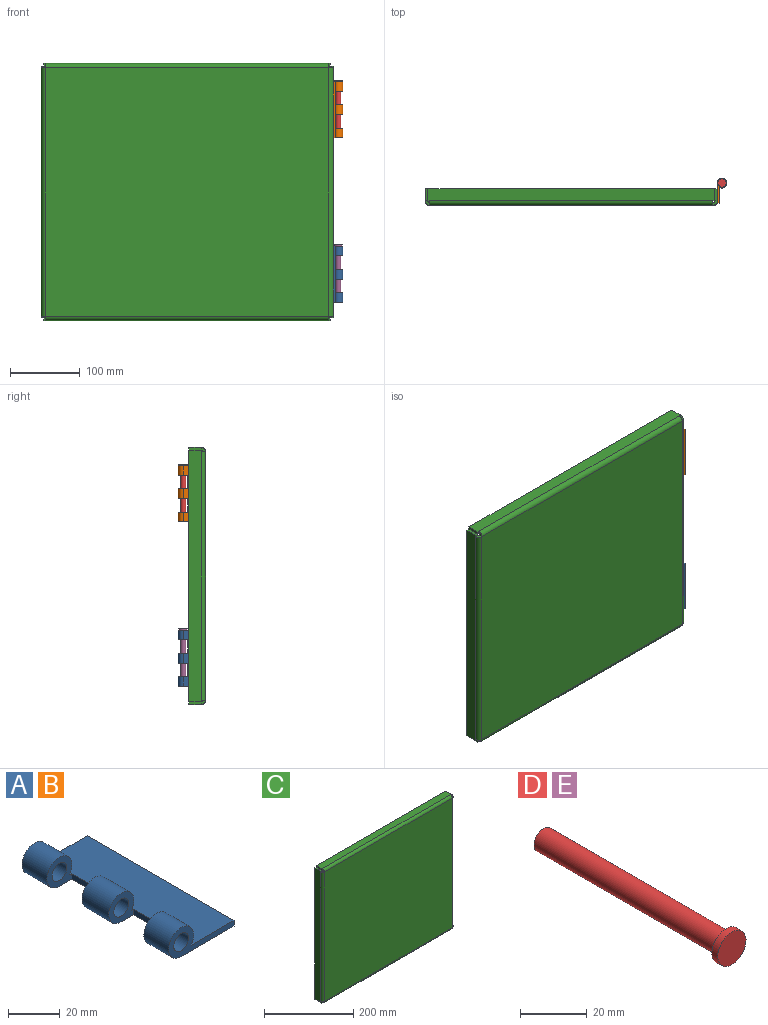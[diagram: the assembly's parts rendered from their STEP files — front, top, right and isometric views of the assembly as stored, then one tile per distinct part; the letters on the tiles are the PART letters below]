
ASSEMBLY  parts=5 mates=4
PART A: 17 faces, bbox 35.7x80x13.7 mm
  f0: plane 80x28.83mm, normal (0,0,-1), area 2044.6mm2, adj f2,f3,f5,f6,f8,f9,f10,f11
  f1: plane 80x23.43mm, normal (0,0,1), area 1819.5mm2, adj f2,f3,f5,f6,f8,f9,f10,f11
  f2: cylinder r=6.83mm len=14.6mm, axis (0,-1,0), area 535.2mm2, adj f0,f1,f12,f15
  f3: cylinder r=6.83mm len=13.65mm, axis (0,-1,0), area 494.8mm2, adj f0,f1,f9,f11
  f4: cylinder r=4.05mm len=13.5mm, axis (0,-1,0), area 343.5mm2, adj f9,f11
  f5: plane 80x2.65mm, normal (1,0,0), area 212mm2, adj f0,f1,f8,f9
  f6: cylinder r=6.83mm len=13.65mm, axis (0,-1,0), area 498.5mm2, adj f0,f1,f8,f14
  f7: cylinder r=4.05mm len=13.6mm, axis (0,-1,0), area 346.1mm2, adj f8,f14
  f8: plane 35.65x13.65mm, normal (0,1,0), area 161.2mm2, adj f0,f1,f5,f6,f7
  f9: plane 35.65x13.65mm, normal (0,-1,0), area 161.2mm2, adj f0,f1,f3,f4,f5
  f10: plane 19.15x2.65mm, normal (-1,0,0), area 50.7mm2, adj f0,f1,f11,f12
  f11: plane 13.65x13.65mm, normal (0,1,0), area 102.9mm2, adj f0,f1,f3,f4,f10
  f12: plane 13.65x13.65mm, normal (0,-1,0), area 102.9mm2, adj f0,f1,f2,f10,f16
  f13: plane 19.15x2.65mm, normal (-1,0,0), area 50.7mm2, adj f0,f1,f14,f15
  f14: plane 13.65x13.65mm, normal (0,-1,0), area 102.9mm2, adj f0,f1,f6,f7,f13
  f15: plane 13.65x13.65mm, normal (0,1,0), area 102.9mm2, adj f0,f1,f2,f13,f16
  f16: cylinder r=4.05mm len=14.6mm, axis (0,-1,0), area 371.5mm2, adj f12,f15
PART B: same geometry as A
PART C: 46 faces, bbox 418x24x368 mm
  f0: plane 4x2.28mm, normal (0,-1,0), area 9.1mm2, adj f4,f5,f6,f42
  f1: plane 4x2.28mm, normal (0,-1,0), area 9.1mm2, adj f2,f5,f6,f43
  f2: plane 17.7x4mm, normal (-1,0,0), area 70.8mm2, adj f1,f3,f5,f6
  f3: plane 409.96x4mm, normal (0,1,0), area 1639.8mm2, adj f2,f4,f5,f6
  f4: plane 17.7x4mm, normal (1,0,0), area 70.8mm2, adj f0,f3,f5,f6
  f5: plane 409.96x17.7mm, normal (0,0,-1), area 7256.3mm2, adj f0,f1,f2,f3,f4,f44
  f6: plane 409.96x17.7mm, normal (0,0,1), area 7256.3mm2, adj f0,f1,f2,f3,f4,f45
  f7: plane 405.4x355.4mm, normal (0,-1,0), area 144079.2mm2, adj f18,f29,f40,f44
  f8: plane 405.4x355.4mm, normal (0,1,0), area 144079.2mm2, adj f19,f30,f41,f45
  f9: plane 4x2.28mm, normal (0,-1,0), area 9.1mm2, adj f13,f14,f15,f17
  f10: plane 4x2.28mm, normal (0,-1,0), area 9.1mm2, adj f11,f14,f15,f16
  f11: plane 17.7x4mm, normal (1,0,0), area 70.8mm2, adj f10,f12,f14,f15
  f12: plane 409.96x4mm, normal (0,1,0), area 1639.8mm2, adj f11,f13,f14,f15
  f13: plane 17.7x4mm, normal (-1,0,0), area 70.8mm2, adj f9,f12,f14,f15
  f14: plane 409.96x17.7mm, normal (0,0,1), area 7256.3mm2, adj f9,f10,f11,f12,f13,f18
  f15: plane 409.96x17.7mm, normal (0,0,-1), area 7256.3mm2, adj f9,f10,f11,f12,f13,f19
  f16: plane 6.3x6.3mm, normal (1,0,0), area 27mm2, adj f10,f18,f19,f38
  f17: plane 6.3x6.3mm, normal (-1,0,0), area 27mm2, adj f9,f18,f19,f27
  f18: cylinder r=6.3mm len=405.4mm, axis (1,0,0), area 4011.8mm2, adj f7,f14,f16,f17
  f19: cylinder r=2.3mm len=405.4mm, axis (1,0,0), area 1464.6mm2, adj f8,f15,f16,f17
  f20: plane 4x2.28mm, normal (0,-1,0), area 9.1mm2, adj f24,f25,f26,f28
  f21: plane 4x2.28mm, normal (0,-1,0), area 9.1mm2, adj f22,f25,f26,f27
  f22: plane 17.7x4mm, normal (0,0,1), area 70.8mm2, adj f21,f23,f25,f26
  f23: plane 359.96x4mm, normal (0,1,0), area 1439.8mm2, adj f22,f24,f25,f26
  f24: plane 17.7x4mm, normal (0,0,-1), area 70.8mm2, adj f20,f23,f25,f26
  f25: plane 359.96x17.7mm, normal (-1,0,0), area 6371.3mm2, adj f20,f21,f22,f23,f24,f29
  f26: plane 359.96x17.7mm, normal (1,0,0), area 6371.3mm2, adj f20,f21,f22,f23,f24,f30
  f27: plane 6.3x6.3mm, normal (0,0,1), area 27mm2, adj f17,f21,f29,f30
  f28: plane 6.3x6.3mm, normal (0,0,-1), area 27mm2, adj f20,f29,f30,f43
  f29: cylinder r=6.3mm len=355.4mm, axis (0,0,1), area 3517mm2, adj f7,f25,f27,f28
  f30: cylinder r=2.3mm len=355.4mm, axis (0,0,1), area 1284mm2, adj f8,f26,f27,f28
  f31: plane 4x2.28mm, normal (0,-1,0), area 9.1mm2, adj f35,f36,f37,f38
  f32: plane 4x2.28mm, normal (0,-1,0), area 9.1mm2, adj f33,f36,f37,f39
  f33: plane 17.7x4mm, normal (0,0,-1), area 70.8mm2, adj f32,f34,f36,f37
  f34: plane 359.96x4mm, normal (0,1,0), area 1439.8mm2, adj f33,f35,f36,f37
  f35: plane 17.7x4mm, normal (0,0,1), area 70.8mm2, adj f31,f34,f36,f37
  f36: plane 359.96x17.7mm, normal (1,0,0), area 6371.3mm2, adj f31,f32,f33,f34,f35,f40
  f37: plane 359.96x17.7mm, normal (-1,0,0), area 6371.3mm2, adj f31,f32,f33,f34,f35,f41
  f38: plane 6.3x6.3mm, normal (0,0,1), area 27mm2, adj f16,f31,f40,f41
  f39: plane 6.3x6.3mm, normal (0,0,-1), area 27mm2, adj f32,f40,f41,f42
  f40: cylinder r=6.3mm len=355.4mm, axis (0,0,1), area 3517mm2, adj f7,f36,f38,f39
  f41: cylinder r=2.3mm len=355.4mm, axis (0,0,1), area 1284mm2, adj f8,f37,f38,f39
  f42: plane 6.3x6.3mm, normal (1,0,0), area 27mm2, adj f0,f39,f44,f45
  f43: plane 6.3x6.3mm, normal (-1,0,0), area 27mm2, adj f1,f28,f44,f45
  f44: cylinder r=6.3mm len=405.4mm, axis (1,0,0), area 4011.8mm2, adj f5,f7,f42,f43
  f45: cylinder r=2.3mm len=405.4mm, axis (1,0,0), area 1464.6mm2, adj f6,f8,f42,f43
PART D: 5 faces, bbox 12x80x12 mm
  f0: cylinder r=4mm len=77.5mm, axis (0,1,0), area 1947.8mm2, adj f1,f4
  f1: plane 8x8mm, normal (0,1,0), area 50.3mm2, adj f0
  f2: cylinder r=6mm len=12mm, axis (0,1,0), area 94.2mm2, adj f3,f4
  f3: plane 12x12mm, normal (0,-1,0), area 113.1mm2, adj f2
  f4: plane 12x12mm, normal (0,1,0), area 62.8mm2, adj f0,f2
PART E: same geometry as D
PLACE A rot(axis=(-0.58,0.58,-0.58),120deg) t=(414,-20.7,102.3)mm
PLACE B rot(axis=(-0.58,0.58,-0.58),120deg) t=(414,-20.7,337.7)mm
PLACE C at identity
PLACE D rot(axis=(0,-0.71,0.71),180deg) t=(420.82,8.12,260.2)mm
PLACE E rot(axis=(0,-0.71,0.71),180deg) t=(420.82,8.13,24.8)mm
MATE fastened A.f0 <-> C.f36  axis (-1,0,0) through (414,-20.7,22.3)mm
MATE revolute D.f0 <-> B.f2  axis (0,0,-1) through (420.82,8.12,337.7)mm
MATE fastened B.f0 <-> C.f36  axis (-1,0,0) through (414,-20.7,337.7)mm
MATE revolute E.f0 <-> A.f2  axis (0,0,-1) through (420.82,8.13,102.3)mm
